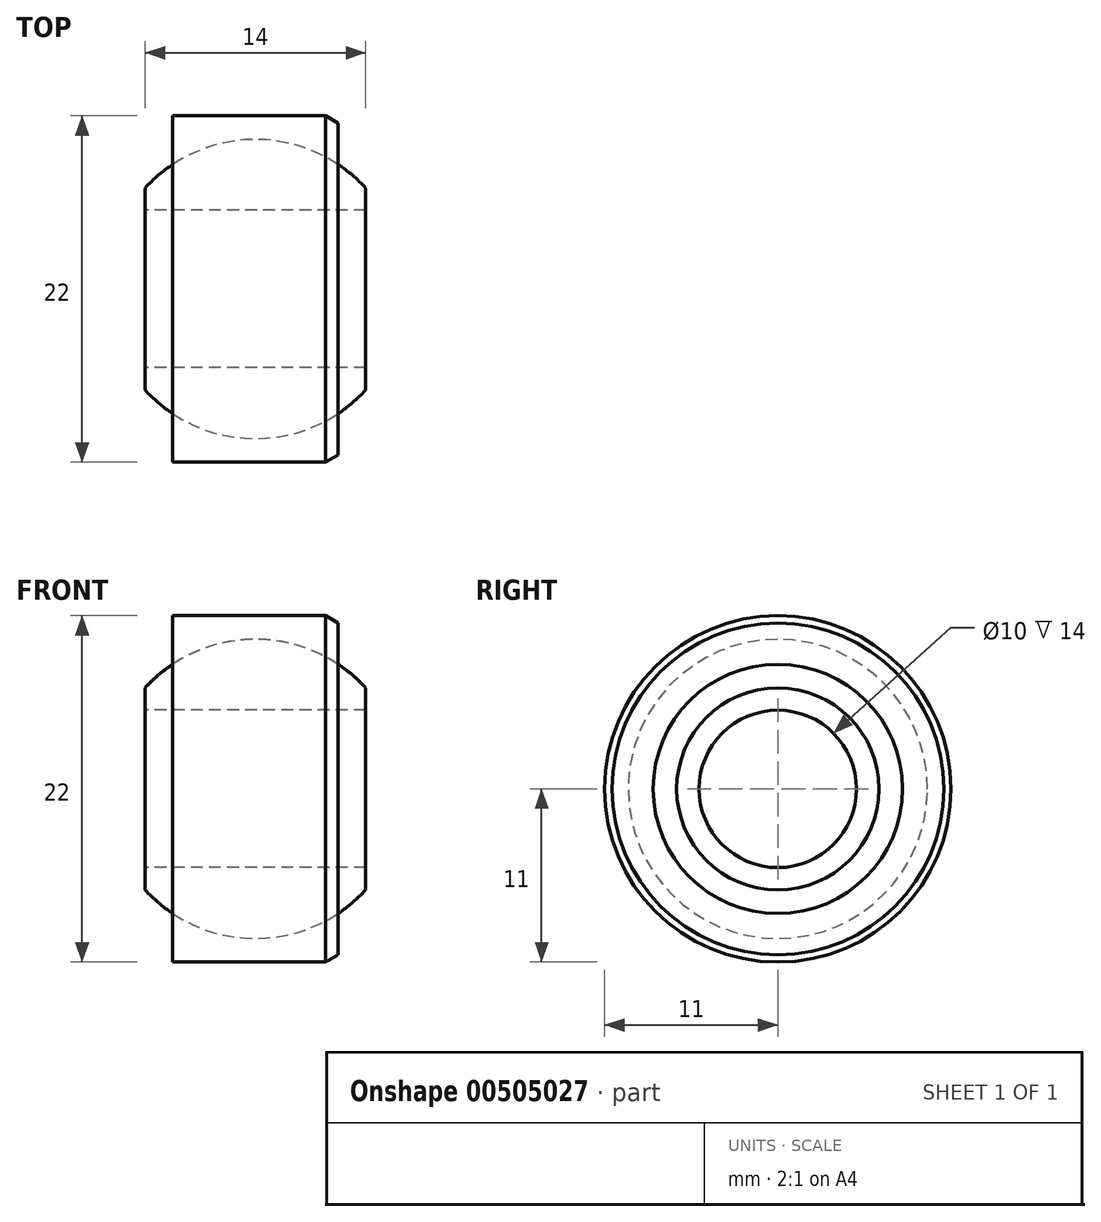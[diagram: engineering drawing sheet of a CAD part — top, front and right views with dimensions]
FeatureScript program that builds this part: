
annotation { "Feature Type Name" : "Feature", "Feature Type Description" : "" }
export const myFeature = defineFeature(function(context is Context, id is Id, definition is map)
    precondition{}
    {
        {
            var Q0;
            Q0=qCreatedBy(makeId("Front.planeOp"),FACE);
            var sketch = newSketch(context, id + "F0", { "sketchPlane" : qUnion([Q0])});
            skArc(sketch, "E0", {"start": v(7, 6.42) * mm, "mid": v(0, 9.5) * mm, "end": v(-7, 6.42) * mm});
            skLineSegment(sketch, "E1.bottom", {"start": v(-7, 5) * mm, "end": v(7, 5) * mm});
            skLineSegment(sketch, "E2", {"start": v(7, 6.42) * mm, "end": v(7, 5) * mm});
            skLineSegment(sketch, "E3", {"start": v(-7, 6.42) * mm, "end": v(-7, 5) * mm});
            skLineSegment(sketch, "E4", {"start": v(-14.22, 0) * mm, "end": v(11.97, 0) * mm});
            skLineSegment(sketch, "E5.bottom", {"start": v(-5.25, 11) * mm, "end": v(5.25, 11) * mm});
            skLineSegment(sketch, "E5.left", {"start": v(-5.25, 11) * mm, "end": v(-5.25, 5) * mm});
            skLineSegment(sketch, "E5.right", {"start": v(5.25, 11) * mm, "end": v(5.25, 5) * mm});
            skPoint(sketch, "E6.orphan", {"position": v(-5.25, -11) * mm});
            skPoint(sketch, "E7.orphan", {"position": v(5.25, -11) * mm});
            skSolve(sketch);
        }
        {
            var Q0;
            Q0=makeQuery(id+"F0.imprint","IMPRINT",FACE,{"disambiguationData":[TD([[makeQuery(id+"F0.imprint","IMPRINT",EDGE,{"derivedFrom":sQuery(id+"F0.wireOp",EDGE,"E0")}),1.0]])]});
            var Q1;
            Q1=sQuery(id+"F0.wireOp",EDGE,"E4");
            revolve(context, id + "F1", {"entities" : qUnion([Q0]), "axis" : qUnion([Q1]), "revolveType" : RevolveType.FULL});
        }
        {
            var Q0;
            {var subQ5=sQuery(id+"F0.wireOp",EDGE,"E5.bottom");Q0=makeQuery(id+"F0.imprint","IMPRINT",FACE,{"disambiguationData":[TD([[makeQuery(id+"F0.imprint","IMPRINT",EDGE,{"derivedFrom":subQ5}),-1.0]])]});}
            var Q1;
            Q1=sQuery(id+"F0.wireOp",EDGE,"E4");
            revolve(context, id + "F2", {"entities" : qUnion([Q0]), "axis" : qUnion([Q1]), "revolveType" : RevolveType.FULL});
        }
        {
            var Q0;
            Q0=makeQuery(id+"F2.opRevolve","SWEPT_EDGE",EDGE,{"disambiguationData":[OSD([sQuery(id+"F0.wireOp",EDGE,"E5.bottom"),sQuery(id+"F0.wireOp",EDGE,"E5.right")])]});
            chamfer(context, id + "F3", {"entities" : qUnion([Q0]), "chamferType" : ChamferType.OFFSET_ANGLE, "width" : 0.8 * mm, "oppositeDirection" : false, "angle" : 30 * degree, "tangentPropagation" : true});
        }
    });
